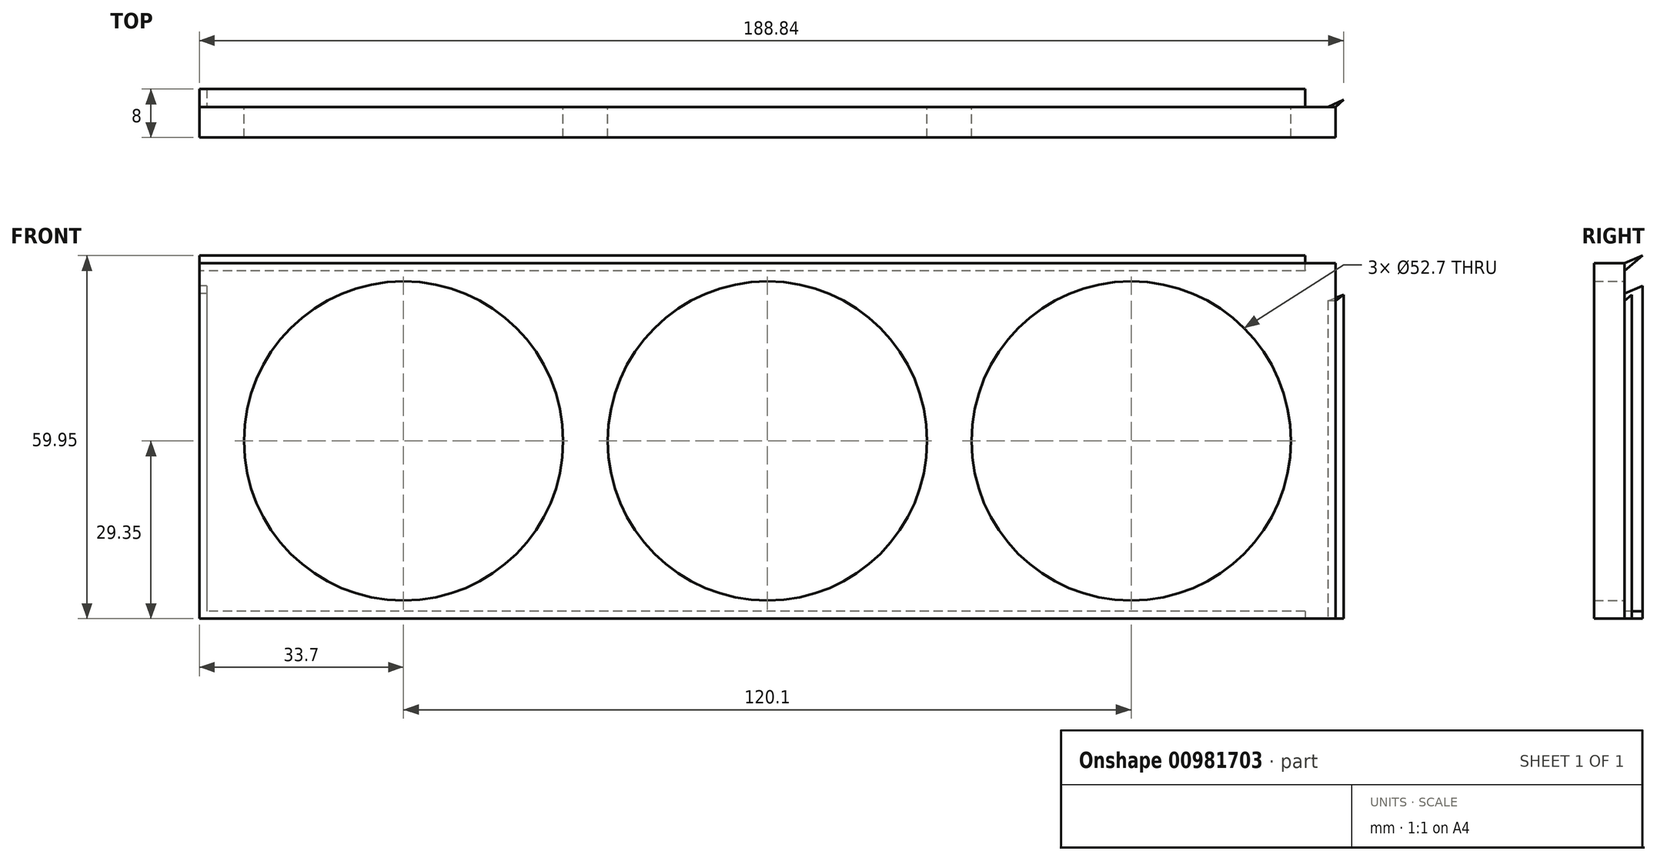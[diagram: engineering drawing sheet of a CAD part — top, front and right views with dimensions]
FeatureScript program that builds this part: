
annotation { "Feature Type Name" : "Feature", "Feature Type Description" : "" }
export const myFeature = defineFeature(function(context is Context, id is Id, definition is map)
    precondition{}
    {
        {
            var Q0;
            Q0=qCreatedBy(makeId("Front.planeOp"),FACE);
            var sketch = newSketch(context, id + "F0", { "sketchPlane" : qUnion([Q0])});
            skLineSegment(sketch, "E0.bottom", {"start": v(0, 0) * mm, "end": v(187.5, 0) * mm});
            skLineSegment(sketch, "E0.top", {"start": v(0, 58.7) * mm, "end": v(187.5, 58.7) * mm});
            skLineSegment(sketch, "E0.left", {"start": v(0, 0) * mm, "end": v(0, 58.7) * mm});
            skLineSegment(sketch, "E0.right", {"start": v(187.5, 0) * mm, "end": v(187.5, 58.7) * mm});
            skSolve(sketch);
        }
        {
            var Q0;
            Q0 = qSketchRegion(id + "F0", true);
            extrude(context, id + "F1", {"entities" : qUnion([Q0]), "depth" : 5 * mm, "offsetDistance" : 25.4 * mm});
        }
        {
            var Q0;
            Q0=qCreatedBy(makeId("Front.planeOp"),FACE);
            var sketch = newSketch(context, id + "F2", { "sketchPlane" : qUnion([Q0])});
            skCircle(sketch, "E1", {"center": v(33.7, 29.35) * mm, "radius": 26.35 * mm});
            skCircle(sketch, "E2", {"center": v(93.75, 29.35) * mm, "radius": 26.35 * mm});
            skCircle(sketch, "E3", {"center": v(153.8, 29.35) * mm, "radius": 26.35 * mm});
            skPoint(sketch, "E4", {"position": v(-64, 101.2) * mm});
            skLineSegment(sketch, "E5", {"start": v(0, 29.35) * mm, "end": v(67.4, 29.35) * mm, "construction": true});
            skLineSegment(sketch, "E6", {"start": v(187.5, 29.35) * mm, "end": v(120.1, 29.35) * mm, "construction": true});
            skSolve(sketch);
        }
        {
            var Q0;
            Q0 = qSketchRegion(id + "F2", true);
            extrude(context, id + "F3", {"entities" : qUnion([Q0]), "operationType" : NewBodyOperationType.REMOVE, "depth" : 25.4 * mm, "offsetDistance" : 25.4 * mm});
        }
        {
            var Q0;
            Q0=qCreatedBy(makeId("Right.planeOp"),FACE);
            var sketch = newSketch(context, id + "F4", { "sketchPlane" : qUnion([Q0])});
            skLineSegment(sketch, "E7", {"start": v(-28.07, 29.35) * mm, "end": v(28.07, 29.35) * mm, "construction": true});
            skLineSegment(sketch, "E8.MirrorCS", {"start": v(0, 58.7) * mm, "end": v(0, 57.45) * mm});
            skLineSegment(sketch, "E9.MirrorCS", {"start": v(3, 59.95) * mm, "end": v(0, 58.7) * mm});
            skLineSegment(sketch, "E10.MirrorCS", {"start": v(0, 57.45) * mm, "end": v(3, 59.95) * mm});
            skLineSegment(sketch, "E11.bottom", {"start": v(0, 0) * mm, "end": v(3, 0) * mm});
            skLineSegment(sketch, "E11.top", {"start": v(0, 1.25) * mm, "end": v(3, 1.25) * mm});
            skLineSegment(sketch, "E11.left", {"start": v(0, 0) * mm, "end": v(0, 1.25) * mm});
            skLineSegment(sketch, "E11.right", {"start": v(3, 0) * mm, "end": v(3, 1.25) * mm});
            skLineSegment(sketch, "E12", {"start": v(3, 62.51) * mm, "end": v(3, -7.16) * mm, "construction": true});
            skSolve(sketch);
        }
        {
            var Q0;
            Q0 = qSketchRegion(id + "F4", true);
            var Q1;
            Q1=makeQuery(id+"F1.opExtrude","SWEPT_FACE",FACE,{"disambiguationData":[OSD([sQuery(id+"F0.wireOp",EDGE,"E0.right")])]});
            extrude(context, id + "F5", {"entities" : qUnion([Q0]), "operationType" : NewBodyOperationType.ADD, "endBound" : BoundingType.UP_TO_SURFACE, "depth" : 25 * mm, "endBoundEntityFace" : qUnion([Q1]), "hasOffset" : true, "offsetDistance" : 5 * mm});
        }
        {
            var Q0;
            Q0=qCreatedBy(makeId("Top.planeOp"),FACE);
            var sketch = newSketch(context, id + "F6", { "sketchPlane" : qUnion([Q0])});
            skLineSegment(sketch, "E13.bottom", {"start": v(0, 0) * mm, "end": v(1.25, 0) * mm});
            skLineSegment(sketch, "E13.top", {"start": v(0, 3) * mm, "end": v(1.25, 3) * mm});
            skLineSegment(sketch, "E13.left", {"start": v(0, 0) * mm, "end": v(0, 3) * mm});
            skLineSegment(sketch, "E13.right", {"start": v(1.25, 0) * mm, "end": v(1.25, 3) * mm});
            skSolve(sketch);
        }
        {
            var Q0;
            Q0 = qSketchRegion(id + "F6", true);
            var Q1;
            Q1=makeQuery(id+"F5.opExtrude","SWEPT_FACE",FACE,{"disambiguationData":[OSD([sQuery(id+"F4.wireOp",EDGE,"E9.MirrorCS")])]});
            extrude(context, id + "F7", {"entities" : qUnion([Q0]), "operationType" : NewBodyOperationType.ADD, "endBound" : BoundingType.UP_TO_SURFACE, "depth" : 25 * mm, "endBoundEntityFace" : qUnion([Q1]), "hasOffset" : true, "offsetDistance" : 5 * mm});
        }
        {
            var Q0;
            Q0=qCreatedBy(makeId("Top.planeOp"),FACE);
            var sketch = newSketch(context, id + "F8", { "sketchPlane" : qUnion([Q0])});
            skLineSegment(sketch, "E14", {"start": v(186.25, 0) * mm, "end": v(188.84, 1.25) * mm});
            skLineSegment(sketch, "E15", {"start": v(188.84, 1.25) * mm, "end": v(187.5, 0) * mm});
            skLineSegment(sketch, "E16", {"start": v(187.5, 0) * mm, "end": v(186.25, 0) * mm});
            skLineSegment(sketch, "E17", {"start": v(188.84, 12.25) * mm, "end": v(188.84, -19.1) * mm, "construction": true});
            skSolve(sketch);
        }
        {
            var Q0;
            Q0 = qSketchRegion(id + "F8", true);
            var Q1;
            Q1=makeQuery(id+"F5.opExtrude","SWEPT_FACE",FACE,{"disambiguationData":[OSD([sQuery(id+"F4.wireOp",EDGE,"E10.MirrorCS")])]});
            extrude(context, id + "F9", {"entities" : qUnion([Q0]), "operationType" : NewBodyOperationType.ADD, "endBound" : BoundingType.UP_TO_SURFACE, "depth" : 25 * mm, "endBoundEntityFace" : qUnion([Q1]), "hasOffset" : true, "offsetDistance" : 5 * mm});
        }
    });
